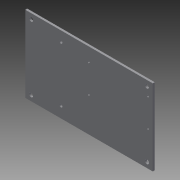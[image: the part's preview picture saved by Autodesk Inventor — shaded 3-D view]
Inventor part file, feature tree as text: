
AUTODESK INVENTOR PART (.ipt)
format: ipt  version: 2014 (Build 180170000, 170)  size: 120,320 bytes
history: native  units: mm
features: extrude x3, sketch x3
ambient origin geometry x8: Origin, YZ Plane, XZ Plane, XY Plane, X Axis, Y Axis, Z Axis, Center Point
bodies: Solid1 (feature_tree)
feature tree (6):
  extrude  "Extrusion1"  Depth=127.0mm
  extrude  "Extrusion2"  Depth=2.0mm
  extrude  "Extrusion3"  Depth=10.0mm
  sketch  "Sketch1"  dims[d0=76.0mm d1=127.0mm]
  sketch  "Sketch2"  dims[d2=2.0mm d3=0.0mm d5=32.6mm]
  sketch  "Sketch3"  dims[d6=57.7mm d7=4.0mm d8=10.0mm d9=0.0mm d10=93.0mm d12=51.0mm d13=10.0mm d14=63.0mm d15=35.0mm d16=11.0mm d17=3.0mm d18=20.0mm d20=55.0mm d21=10.0mm d23=10.0mm d25=32.0mm d26=29.5mm d27=2.0mm d28=15.0mm d29=20.0mm d31=28.0mm d32=20.0mm d34=58.9mm d37=10.0mm d38=0.0mm]
